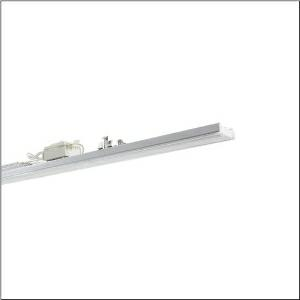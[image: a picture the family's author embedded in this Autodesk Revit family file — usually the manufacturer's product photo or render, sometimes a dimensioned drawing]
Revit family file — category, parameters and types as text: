
# Revit family: licross_11_recessed_mo_51tl12mn4axg
name_source: partatom
category: Lighting Fixtures
units: mm (PartAtom-declared; Revit-internal decimal feet)

## family parameters
Cut with Voids When Loaded = No
Host = Face
Light Source = No
Part Type = Normal
Room Calculation Point = No
Round Connector Dimension = Use Diameter
Shared = No

## types (1)
- --- (1 x LED, 10290 lm, 55.2 W, 4000K)
    Apparent Load = 55 VA
    CIE Flux Codes = 67 92 99 100 100
    Color Rendering = 80
    Color Temperature = 4000K
    Default Elevation = 1800 mm
    Description = Licross 11 Recessed MO, luminaire insert, of sheet steel, coil coated, white, length: 1.500mm, width: 66mm, height: 67mm, LED rated luminous flux: 10.290lm, light colour: 840, SDCM (Standard Deviation of Colour Matching)MacAdam ≤ 2 SDCM (initial), control gear: ON/OFF Multilumen, with plug, 3-pole, with phase selection, mains connection: 220..240V, AC, 50/60Hz, rated input power: 55W, internal wiring halogen-free, primary optical cover: cover, of PMMA, light emission: direct distribution, primary light characteristic: symmetric, protection rating (complete): IP40, insulation class (complete): insulation class I (protective earthing), certification: CE, ENEC, VDE, UKCA, protection symbol: D if used in an environment without relevant dust loads with corresponding accessories, impact resistance: IK06, permissible ambient temperature for indoor applications: -35..+40°C, corresponds to IFS (International Featured Standards) requirements for safety and quality in the food industry, reducing of maximum allowable ambient temperature of 5°C with ceiling mounting, The light source and the operating device comply with the requirements of the Ecodesign Regulation (EU) 2019/2020 and are replaceable in accordance with this regulation, packaging unit: 1 piece
    Height = 58 mm
    Lamp = 1 x LED
    Lamp Light Flux = 10290 lm
    Lamp Power = 55.2 W
    Lamp count = 1
    Length = 1500 mm
    Luminous efficacy = 186 lm/W
    Manufacturer = Siteco
    ModVariant = No
    Model = 51TL12MN4AXG
    Mounting Place = Ceiling
    Mounting Type = Pendant
    Number of Poles = 1
    OnlyDefault = Yes
    Power Factor = 1
    Product Name = Licross 11 Recessed MO
    Product group = luminaire insert | ceiling pendant
    ProductGroupID = 901
    Protection Class = Protection class I
    Protection Degree = IP 40
    RLX_Detail_Level = 1
    RLX_Emergency_Light_Flux = 0 lm
    RLX_Emergency_Type = 0
    RLX_Emergency_Type_DB = No
    RlxData = <blob elided: 22369 chars, md5=5c5e969f>
    Socket = socket
    Standby Power = 0 W
    System Light Flux = 10290 lm
    System Power = 55 W
    Type Comments = factory setting: luminous flux: 100 % | (A | C | E) | 126 mA
    Type Image = l_1296930.jpg
    URL = http://relux.com
    VarID = @adj_090301
    Voltage = 0 V
    Weight = 0.00 kg
    Width = 66 mm

## geometry (parser evidence)
native form markers: Blend x4, Sweep x11
no freeform markers — native parametric forms only
